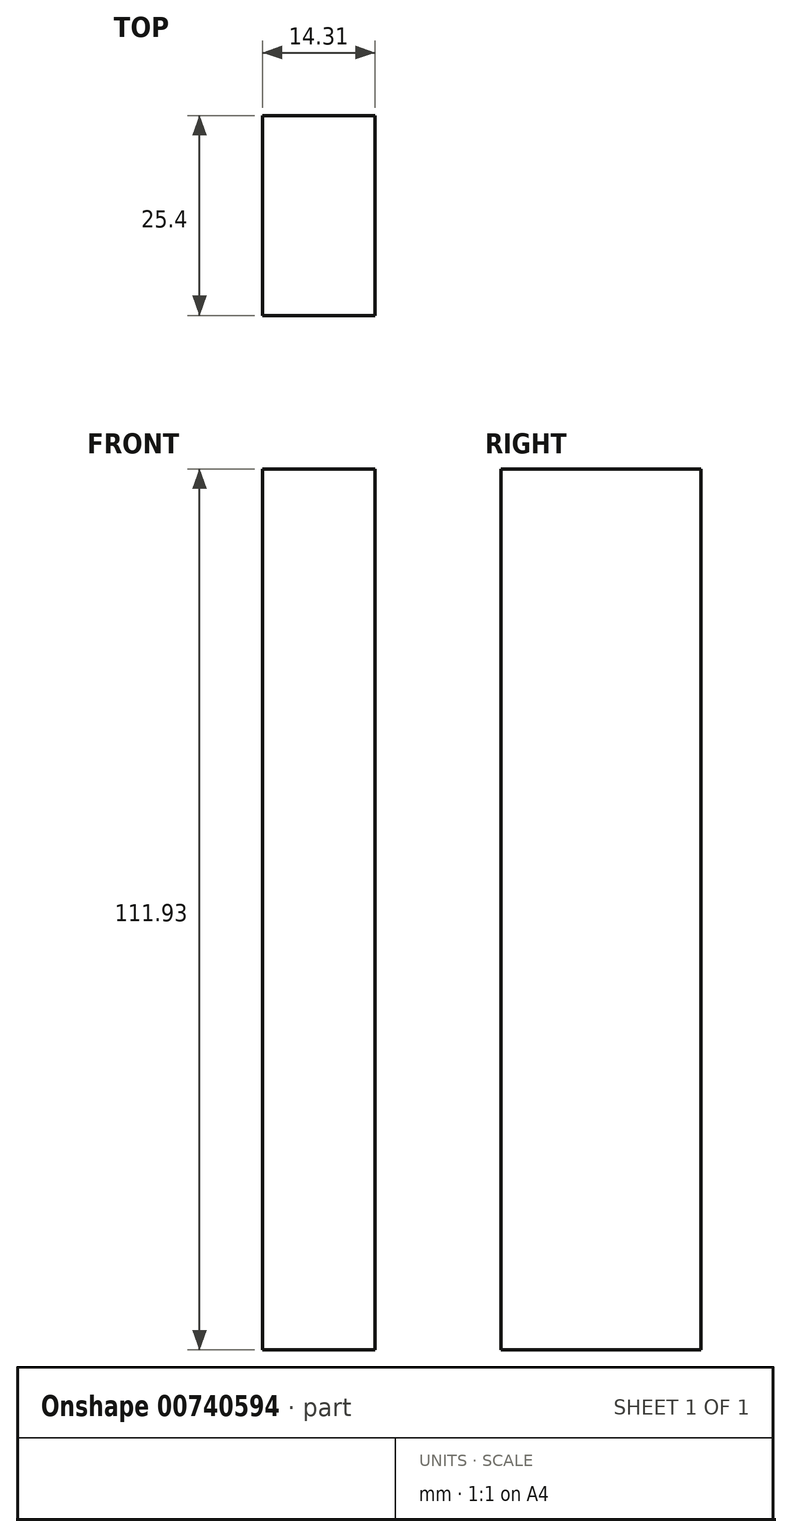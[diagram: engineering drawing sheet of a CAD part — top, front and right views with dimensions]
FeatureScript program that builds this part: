
annotation { "Feature Type Name" : "Feature", "Feature Type Description" : "" }
export const myFeature = defineFeature(function(context is Context, id is Id, definition is map)
    precondition{}
    {
        {
            var Q0;
            Q0=qCreatedBy(makeId("Front.planeOp"),FACE);
            var sketch = newSketch(context, id + "F0", { "sketchPlane" : qUnion([Q0])});
            skLineSegment(sketch, "E0.bottom", {"start": v(-28.84, 42) * mm, "end": v(-14.53, 42) * mm});
            skLineSegment(sketch, "E0.top", {"start": v(-28.84, -69.92) * mm, "end": v(-14.53, -69.92) * mm});
            skLineSegment(sketch, "E0.left", {"start": v(-28.84, 42) * mm, "end": v(-28.84, -69.92) * mm});
            skLineSegment(sketch, "E0.right", {"start": v(-14.53, 42) * mm, "end": v(-14.53, -69.92) * mm});
            skSolve(sketch);
        }
        {
            var Q0;
            Q0 = qSketchRegion(id + "F0", true);
            extrude(context, id + "F1", {"entities" : qUnion([Q0]), "depth" : 25.4 * mm, "offsetDistance" : 25.4 * mm});
        }
    });
